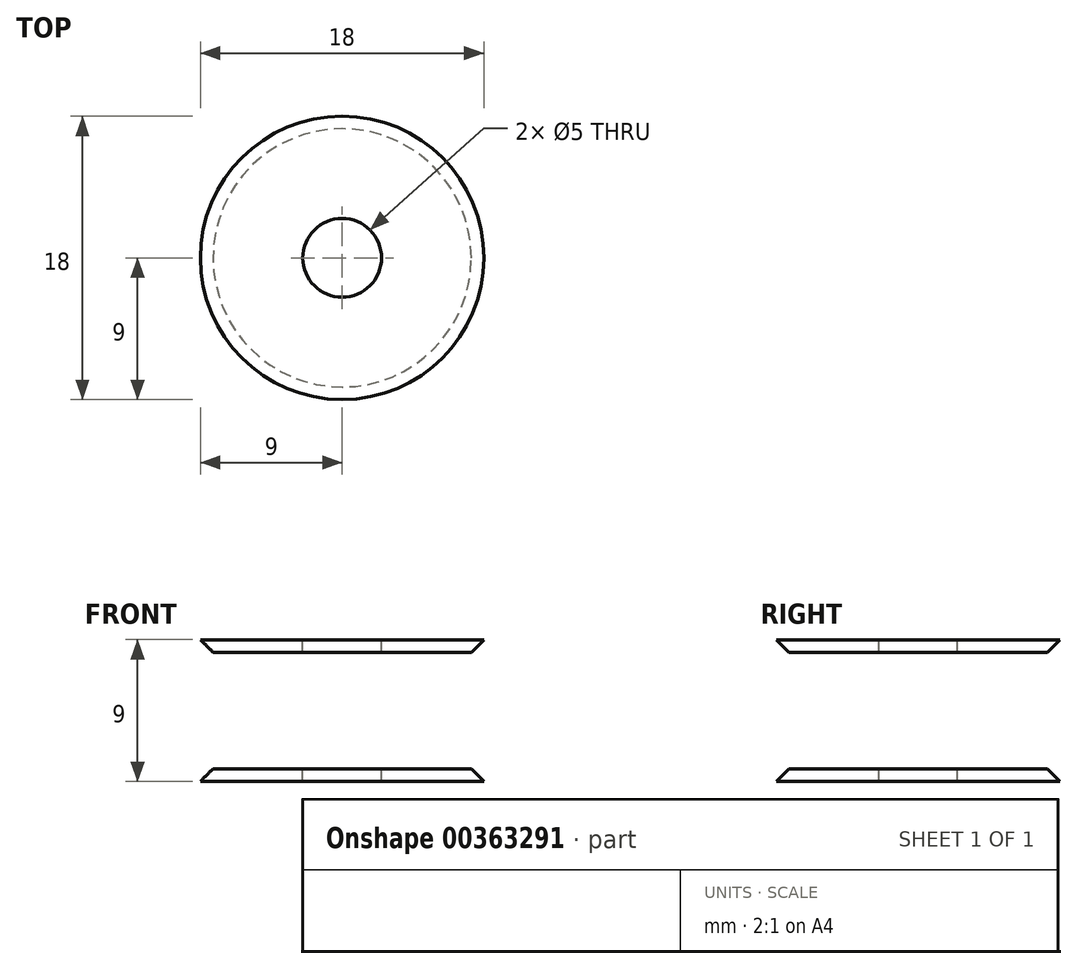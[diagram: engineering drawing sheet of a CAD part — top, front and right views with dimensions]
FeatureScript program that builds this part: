
annotation { "Feature Type Name" : "Feature", "Feature Type Description" : "" }
export const myFeature = defineFeature(function(context is Context, id is Id, definition is map)
    precondition{}
    {
        {
            var Q0;
            Q0=qCreatedBy(makeId("Front.planeOp"),FACE);
            var sketch = newSketch(context, id + "F0", { "sketchPlane" : qUnion([Q0])});
            skLineSegment(sketch, "E0", {"start": v(0, -26.92) * mm, "end": v(0, 33.9) * mm, "construction": true});
            skLineSegment(sketch, "E1", {"start": v(-9, 11.69) * mm, "end": v(0, 11.69) * mm});
            skLineSegment(sketch, "E2", {"start": v(0, 11.69) * mm, "end": v(0, 10.89) * mm});
            skLineSegment(sketch, "E3", {"start": v(0, 10.89) * mm, "end": v(-8.2, 10.89) * mm});
            skLineSegment(sketch, "E4", {"start": v(-8.2, 10.89) * mm, "end": v(-9, 11.69) * mm});
            skLineSegment(sketch, "E5.bottom", {"start": v(0, 10.89) * mm, "end": v(-6, 10.89) * mm});
            skLineSegment(sketch, "E5.top", {"start": v(0, 3.49) * mm, "end": v(-6, 3.49) * mm});
            skLineSegment(sketch, "E5.left", {"start": v(0, 10.89) * mm, "end": v(0, 3.49) * mm});
            skLineSegment(sketch, "E5.right", {"start": v(-6, 10.89) * mm, "end": v(-6, 3.49) * mm});
            skLineSegment(sketch, "E6", {"start": v(-8.2, 3.49) * mm, "end": v(0, 3.49) * mm});
            skLineSegment(sketch, "E7", {"start": v(0, 2.69) * mm, "end": v(-9, 2.69) * mm});
            skLineSegment(sketch, "E8", {"start": v(-9, 2.69) * mm, "end": v(-8.2, 3.49) * mm});
            skLineSegment(sketch, "E9", {"start": v(0, 3.49) * mm, "end": v(0, 2.69) * mm});
            skLineSegment(sketch, "E10", {"start": v(-8.2, 10.89) * mm, "end": v(-9, 10.89) * mm, "construction": true});
            skLineSegment(sketch, "E11", {"start": v(-8.2, 3.49) * mm, "end": v(-9, 3.49) * mm, "construction": true});
            skSolve(sketch);
        }
        {
            var Q0;
            Q0=makeQuery(id+"F0.imprint","IMPRINT",FACE,{"disambiguationData":[TD([[makeQuery(id+"F0.imprint","IMPRINT",EDGE,{"derivedFrom":sQuery(id+"F0.wireOp",EDGE,"E1")}),-1.0]])]});
            var Q1;
            Q1=makeQuery(id+"F0.imprint","IMPRINT",FACE,{"disambiguationData":[TD([[makeQuery(id+"F0.imprint","IMPRINT",EDGE,{"derivedFrom":sQuery(id+"F0.wireOp",EDGE,"E5.bottom")}),1.0]])]});
            var Q2;
            Q2=makeQuery(id+"F0.imprint","IMPRINT",FACE,{"disambiguationData":[TD([[makeQuery(id+"F0.imprint","IMPRINT",EDGE,{"derivedFrom":sQuery(id+"F0.wireOp",EDGE,"E7")}),-1.0]])]});
            var Q3;
            Q3=sQuery(id+"F0.wireOp",EDGE,"E0");
            revolve(context, id + "F1", {"entities" : qUnion([Q0, Q1, Q2]), "axis" : qUnion([Q3]), "revolveType" : RevolveType.FULL});
        }
        {
            var Q0;
            Q0=makeQuery(id+"F1.opRevolve","SWEPT_FACE",FACE,{"disambiguationData":[OSD([sQuery(id+"F0.wireOp",EDGE,"E1")])]});
            var sketch = newSketch(context, id + "F2", { "sketchPlane" : qUnion([Q0])});
            skCircle(sketch, "E12", {"center": v(0, 0) * mm, "radius": 2.5 * mm});
            skSolve(sketch);
        }
        {
            var Q0;
            Q0=makeQuery(id+"F2.imprint","IMPRINT",FACE,{"disambiguationData":[TD([[makeQuery(id+"F2.imprint","IMPRINT",EDGE,{"derivedFrom":sQuery(id+"F2.wireOp",EDGE,"E12")}),1.0]])]});
            var Q1;
            Q1=sQuery(id+"F2.wireOp",EDGE,"E12");
            var Q2;
            Q2=makeQuery(id+"F1.opRevolve","SWEPT_FACE",FACE,{"disambiguationData":[OSD([sQuery(id+"F0.wireOp",EDGE,"E7")])]});
            extrude(context, id + "F3", {"entities" : qUnion([Q0]), "operationType" : NewBodyOperationType.REMOVE, "surfaceEntities" : qUnion([Q1]), "endBound" : BoundingType.UP_TO_SURFACE, "oppositeDirection" : true, "endBoundEntityFace" : qUnion([Q2]), "depth" : 25 * mm});
        }
    });
